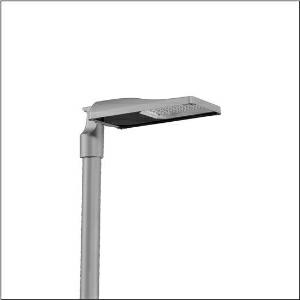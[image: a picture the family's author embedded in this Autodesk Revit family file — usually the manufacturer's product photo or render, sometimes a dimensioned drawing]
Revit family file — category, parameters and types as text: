
# Revit family: streetlight_sl_31_mini___st1_0a_5xh6d31a08ja_4a04
name_source: partatom
category: Lighting Fixtures
units: mm (PartAtom-declared; Revit-internal decimal feet)

## family parameters
Cut with Voids When Loaded = No
Host = Face
Light Source = No
Part Type = Normal
Room Calculation Point = No
Round Connector Dimension = Use Diameter
Shared = No

## types (1)
- --- (1 x LED, 12140 lm, 81.1 W, 3000K)
    Apparent Load = 81 VA
    CIE Flux Codes = 40 73 97 100 100
    Color Rendering = 70
    Color Temperature = 3000K
    Default Elevation = 1800 mm
    Description = Streetlight SL 31 mini Easy, Desk-Remote mast luminaire for post-top, side-entry; light control with lens of PMMA; light distribution: ST1.0a, direct asymmetric distribution, for standard-compliant lighting for roads and squares; LED: luminous flux: 12.140lm, light colour: 730, colour temperature: 3000K; luminous efficacy: 149,7lm/W; control: pre-setting: linear dimming characteristic, flexible luminous flux parameterisation, time-dependent luminous flux control, constant luminous flux control, intelligent temperature release in ECG and LED module, overheat protection; luminaire housing, of diecast aluminium, Siteco® metallic grey (DB 702S), corrosivity category C5 high according to DIN EN ISO 12944; cover of toughened safety glass, transparent, opened without tools; mast flange of diecast aluminium, Siteco® metallic grey (DB 702S), spigot size: 76/60mm, mast flange included unmounted; with cable H07RN-F 2x 1.5mm², cable length: 10,5m, connection cable pre-assembled; mains connection: 220..240V, AC, 50/60Hz; power consumption (at start of service life): 81,1W / (at end of service life): 88,3W / (with reduced operation 50%): 36,4W; protection rating (complete): IP66; insulation class (complete): insulation class II (safety insulation); impact resistance: IK10; certification: CE, ENEC, ENEC+, VDE, UKCA; permissible operating ambient temperature for outdoor applications: -40..+50°C; packaging unit: 1 piece

Light Distribution: ST1.0a
    Height = 76 mm
    Lamp = 1 x LED
    Lamp Light Flux = 12140 lm
    Lamp Power = 81.1 W
    Lamp count = 1
    Length = 547 mm
    Luminous efficacy = 150 lm/W
    Manufacturer = Siteco
    ModVariant = No
    Model = 5XH6D31A08JA
    Number of Poles = 1
    OnlyDefault = Yes
    Power Factor = 1
    Product Name = Streetlight SL 31 mini | ST1.0a
    Product group = mast luminaire | pylon top
    ProductGroupID = 6100
    Protection Class = Protection class II
    Protection Degree = IP 66
    RLX_Detail_Level = 1
    RLX_Emergency_Light_Flux = 0 lm
    RLX_Emergency_Type = 0
    RLX_Emergency_Type_DB = No
    RlxData = <blob elided: 39657 chars, md5=32efa880>
    Socket = socket
    Standby Power = 0 W
    System Light Flux = 12140 lm
    System Power = 81 W
    Type Comments = factory setting: luminous flux: 100 % | dim-lin: 254 | 860 mA
    Type Image = l_1300326.jpg
    URL = http://relux.com
    VarID = @adj_050526
    Voltage = 0 V
    Weight = 0.00 kg
    Width = 265 mm

## geometry (parser evidence)
native form markers: Blend x4, Sweep x11
no freeform markers — native parametric forms only
